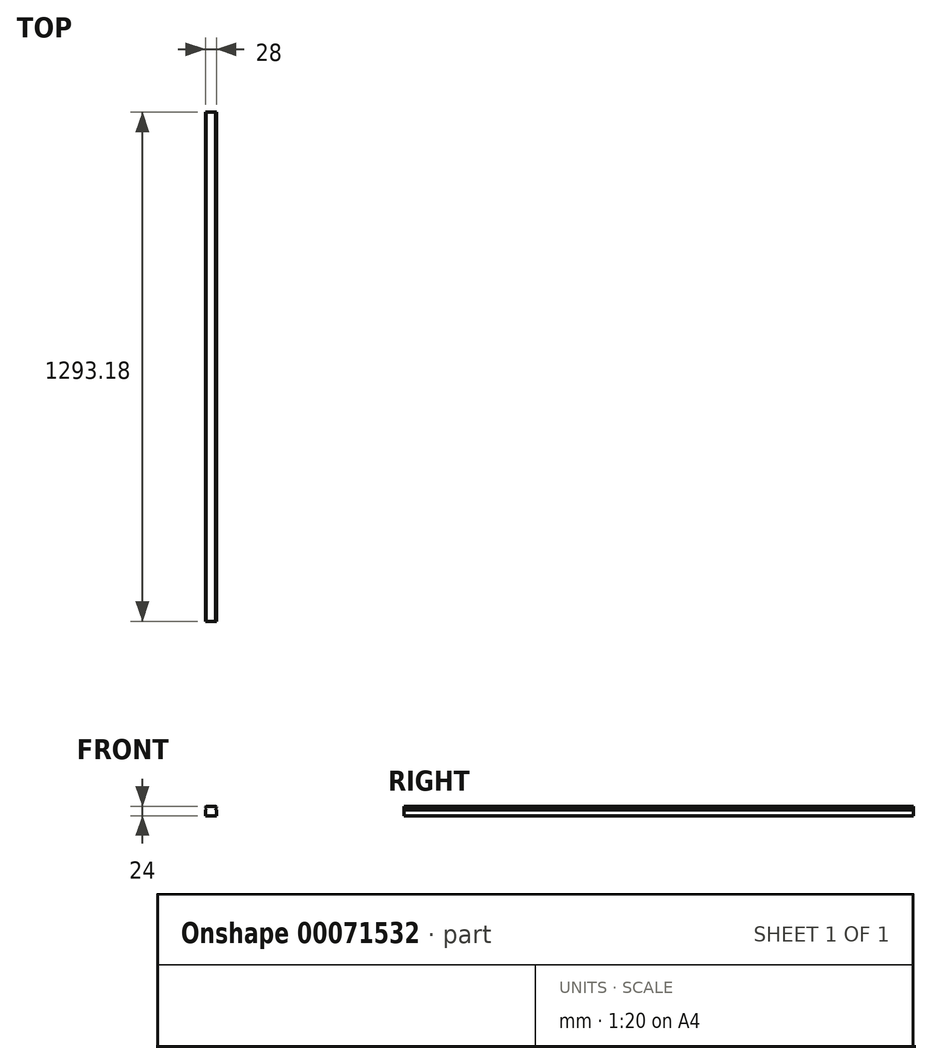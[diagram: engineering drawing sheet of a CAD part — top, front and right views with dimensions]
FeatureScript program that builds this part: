
annotation { "Feature Type Name" : "Feature", "Feature Type Description" : "" }
export const myFeature = defineFeature(function(context is Context, id is Id, definition is map)
    precondition{}
    {
        {
            var Q0;
            Q0=qCreatedBy(makeId("Front.planeOp"),FACE);
            var sketch = newSketch(context, id + "F0", { "sketchPlane" : qUnion([Q0])});
            skLineSegment(sketch, "E0.bottom", {"start": v(-9.9, 12.6) * mm, "end": v(13.87, 12.6) * mm});
            skLineSegment(sketch, "E0.top", {"start": v(-12.01, -11.4) * mm, "end": v(15.99, -11.4) * mm});
            skLineSegment(sketch, "E0.left", {"start": v(-12.01, 10.49) * mm, "end": v(-12.01, 9.49) * mm});
            skLineSegment(sketch, "E0.right", {"start": v(15.99, 10.49) * mm, "end": v(15.99, 9.49) * mm});
            skLineSegment(sketch, "E1", {"start": v(-9.9, 12.6) * mm, "end": v(-12.01, 10.49) * mm});
            skLineSegment(sketch, "E2", {"start": v(13.87, 12.6) * mm, "end": v(15.99, 10.49) * mm});
            skLineSegment(sketch, "E3", {"start": v(-12.01, 9.49) * mm, "end": v(-9.18, 6.66) * mm});
            skLineSegment(sketch, "E4", {"start": v(-9.18, 6.66) * mm, "end": v(-12.01, 3.83) * mm});
            skLineSegment(sketch, "E5", {"start": v(15.99, 9.49) * mm, "end": v(13.16, 6.66) * mm});
            skLineSegment(sketch, "E6", {"start": v(13.16, 6.66) * mm, "end": v(15.99, 3.83) * mm});
            skLineSegment(sketch, "E7.trimOffspring", {"start": v(-12.01, 3.83) * mm, "end": v(-12.01, -11.4) * mm});
            skLineSegment(sketch, "E8.trimOffspring", {"start": v(15.99, 3.83) * mm, "end": v(15.99, -11.4) * mm});
            skSolve(sketch);
        }
        {
            var Q0;
            Q0=qSketchRegion(id+"F0",true);
            extrude(context, id + "F1", {"entities" : qUnion([Q0]), "depth" : 1293.18 * mm});
        }
    });
